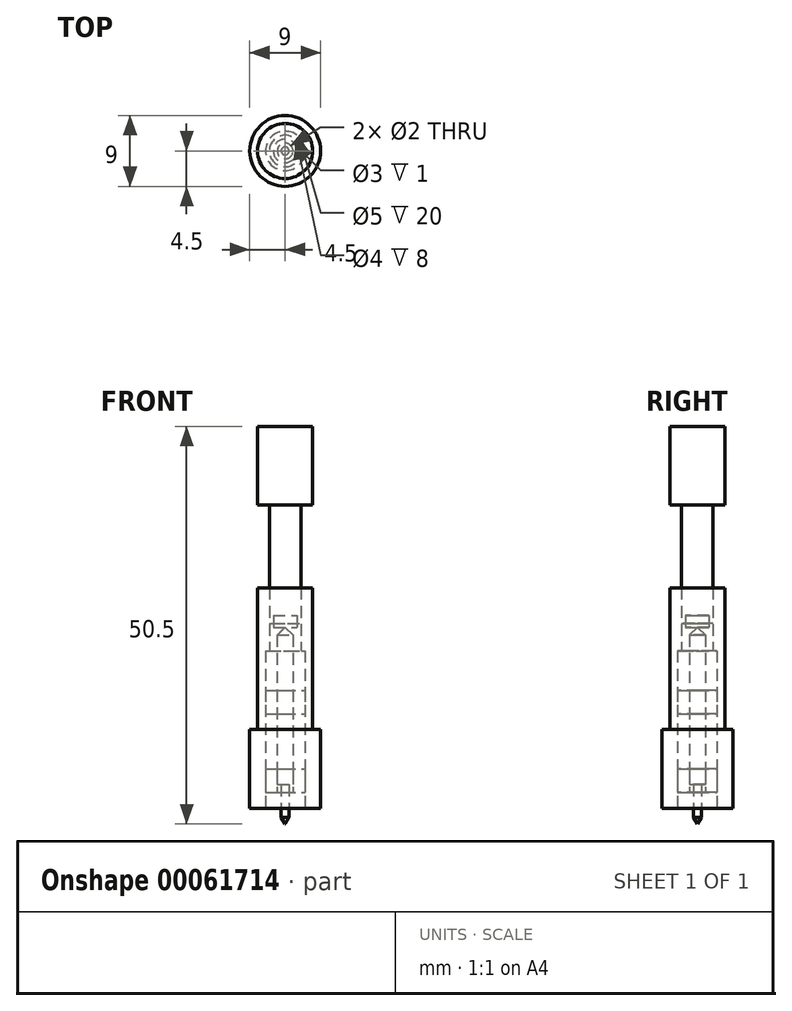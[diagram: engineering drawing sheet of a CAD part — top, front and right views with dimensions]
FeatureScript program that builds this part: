
annotation { "Feature Type Name" : "Feature", "Feature Type Description" : "" }
export const myFeature = defineFeature(function(context is Context, id is Id, definition is map)
    precondition{}
    {
        {
            var Q0;
            Q0=qCreatedBy(makeId("Front.planeOp"),FACE);
            var sketch = newSketch(context, id + "F0", { "sketchPlane" : qUnion([Q0])});
            skLineSegment(sketch, "E0", {"start": v(0, 7.13) * mm, "end": v(-1, 6.13) * mm});
            skLineSegment(sketch, "E1", {"start": v(-1, 6.13) * mm, "end": v(-1, -12.87) * mm});
            skLineSegment(sketch, "E2", {"start": v(-1, -12.87) * mm, "end": v(-0.5, -12.87) * mm});
            skLineSegment(sketch, "E3", {"start": v(-0.5, -12.87) * mm, "end": v(-0.5, -17) * mm});
            skLineSegment(sketch, "E4", {"start": v(-0.5, -17) * mm, "end": v(0, -17.87) * mm});
            skLineSegment(sketch, "E5", {"start": v(0, -17.87) * mm, "end": v(0, 7.13) * mm});
            skLineSegment(sketch, "E6.bottom", {"start": v(-1, -13.87) * mm, "end": v(-2.5, -13.87) * mm});
            skLineSegment(sketch, "E6.top", {"start": v(-1, -10.87) * mm, "end": v(-2.5, -10.87) * mm});
            skLineSegment(sketch, "E6.left", {"start": v(-1, -13.87) * mm, "end": v(-1, -10.87) * mm});
            skLineSegment(sketch, "E6.right", {"start": v(-2.5, -13.87) * mm, "end": v(-2.5, -10.87) * mm});
            skLineSegment(sketch, "E7.bottom", {"start": v(-1, -3.87) * mm, "end": v(-2.5, -3.87) * mm});
            skLineSegment(sketch, "E7.top", {"start": v(-1, -0.87) * mm, "end": v(-2.5, -0.87) * mm});
            skLineSegment(sketch, "E7.right", {"start": v(-2.5, -3.87) * mm, "end": v(-2.5, -0.87) * mm});
            skLineSegment(sketch, "E8", {"start": v(-1, -0.87) * mm, "end": v(-1, -3.87) * mm});
            skLineSegment(sketch, "E9.bottom", {"start": v(0, 7.13) * mm, "end": v(-1.5, 7.13) * mm});
            skLineSegment(sketch, "E9.top", {"start": v(0, 8.63) * mm, "end": v(-1.5, 8.63) * mm});
            skLineSegment(sketch, "E9.left", {"start": v(0, 7.13) * mm, "end": v(0, 8.63) * mm});
            skLineSegment(sketch, "E9.right", {"start": v(-1.5, 7.13) * mm, "end": v(-1.5, 8.63) * mm});
            skLineSegment(sketch, "E10", {"start": v(0, -52.78) * mm, "end": v(0, 70.04) * mm, "construction": true});
            skLineSegment(sketch, "E11", {"start": v(-1.5, 7.63) * mm, "end": v(-2, 7.63) * mm});
            skLineSegment(sketch, "E12", {"start": v(-2, 7.63) * mm, "end": v(-2, 22.63) * mm});
            skLineSegment(sketch, "E13", {"start": v(-2, 22.63) * mm, "end": v(-3.5, 22.63) * mm});
            skLineSegment(sketch, "E14", {"start": v(-3.5, 22.63) * mm, "end": v(-3.5, 32.63) * mm});
            skLineSegment(sketch, "E15", {"start": v(-3.5, 32.63) * mm, "end": v(0, 32.63) * mm});
            skLineSegment(sketch, "E16", {"start": v(0, 32.63) * mm, "end": v(0, 8.63) * mm});
            skLineSegment(sketch, "E17", {"start": v(-2, 12.13) * mm, "end": v(-3.5, 12.13) * mm});
            skLineSegment(sketch, "E18", {"start": v(-3.5, 12.13) * mm, "end": v(-3.5, -5.87) * mm});
            skLineSegment(sketch, "E19", {"start": v(-3.5, -5.87) * mm, "end": v(-4.5, -5.87) * mm});
            skLineSegment(sketch, "E20", {"start": v(-4.5, -5.87) * mm, "end": v(-4.5, -15.87) * mm});
            skLineSegment(sketch, "E21", {"start": v(-4.5, -15.87) * mm, "end": v(-2.5, -15.87) * mm});
            skLineSegment(sketch, "E22", {"start": v(-2.5, -15.87) * mm, "end": v(-2.5, 4.13) * mm});
            skLineSegment(sketch, "E23", {"start": v(-2.5, 4.13) * mm, "end": v(-2, 4.13) * mm});
            skLineSegment(sketch, "E24", {"start": v(-2, 4.13) * mm, "end": v(-2, 12.13) * mm});
            skLineSegment(sketch, "E25", {"start": v(0, 17.09) * mm, "end": v(0, -94.36) * mm, "construction": true});
            skSolve(sketch);
        }
        {
            var Q0;
            Q0=makeQuery(id+"F0.imprint","IMPRINT",FACE,{"disambiguationData":[TD([[makeQuery(id+"F0.imprint","IMPRINT",EDGE,{"derivedFrom":sQuery(id+"F0.wireOp",EDGE,"E0")}),1.0]])]});
            var Q1;
            Q1=sQuery(id+"F0.wireOp",EDGE,"E10");
            revolve(context, id + "F1", {"entities" : qUnion([Q0]), "axis" : qUnion([Q1]), "revolveType" : RevolveType.FULL});
        }
        {
            var Q0;
            Q0=makeQuery(id+"F0.imprint","IMPRINT",FACE,{"disambiguationData":[TD([[makeQuery(id+"F0.imprint","IMPRINT",EDGE,{"derivedFrom":sQuery(id+"F0.wireOp",EDGE,"E7.bottom")}),-1.0]])]});
            var Q1;
            Q1=makeQuery(id+"F0.imprint","IMPRINT",FACE,{"disambiguationData":[TD([[makeQuery(id+"F0.imprint","IMPRINT",EDGE,{"derivedFrom":sQuery(id+"F0.wireOp",EDGE,"E6.bottom")}),-1.0]])]});
            var Q2;
            Q2=sQuery(id+"F0.wireOp",EDGE,"E5");
            revolve(context, id + "F2", {"entities" : qUnion([Q0, Q1]), "axis" : qUnion([Q2]), "revolveType" : RevolveType.FULL});
        }
        {
            var Q0;
            Q0=makeQuery(id+"F0.imprint","IMPRINT",FACE,{"disambiguationData":[TD([[makeQuery(id+"F0.imprint","IMPRINT",EDGE,{"derivedFrom":sQuery(id+"F0.wireOp",EDGE,"E9.bottom")}),-1.0]])]});
            var Q1;
            Q1=sQuery(id+"F0.wireOp",EDGE,"E5");
            revolve(context, id + "F3", {"entities" : qUnion([Q0]), "axis" : qUnion([Q1]), "revolveType" : RevolveType.FULL});
        }
        {
            var Q0;
            {var subQ2=sQuery(id+"F0.wireOp",EDGE,"E9.top");Q0=makeQuery(id+"F0.imprint","IMPRINT",FACE,{"disambiguationData":[TD([[makeQuery(id+"F0.imprint","IMPRINT",EDGE,{"derivedFrom":subQ2}),-1.0]])]});}
            var Q1;
            Q1=sQuery(id+"F0.wireOp",EDGE,"E10");
            revolve(context, id + "F4", {"entities" : qUnion([Q0]), "axis" : qUnion([Q1]), "revolveType" : RevolveType.FULL});
        }
        {
            var Q0;
            {var subQ9=sQuery(id+"F0.wireOp",EDGE,"E17");Q0=makeQuery(id+"F0.imprint","IMPRINT",FACE,{"disambiguationData":[TD([[makeQuery(id+"F0.imprint","IMPRINT",EDGE,{"derivedFrom":subQ9}),1.0]])]});}
            var Q1;
            Q1=sQuery(id+"F0.wireOp",EDGE,"E5");
            revolve(context, id + "F5", {"entities" : qUnion([Q0]), "axis" : qUnion([Q1]), "revolveType" : RevolveType.FULL});
        }
    });
